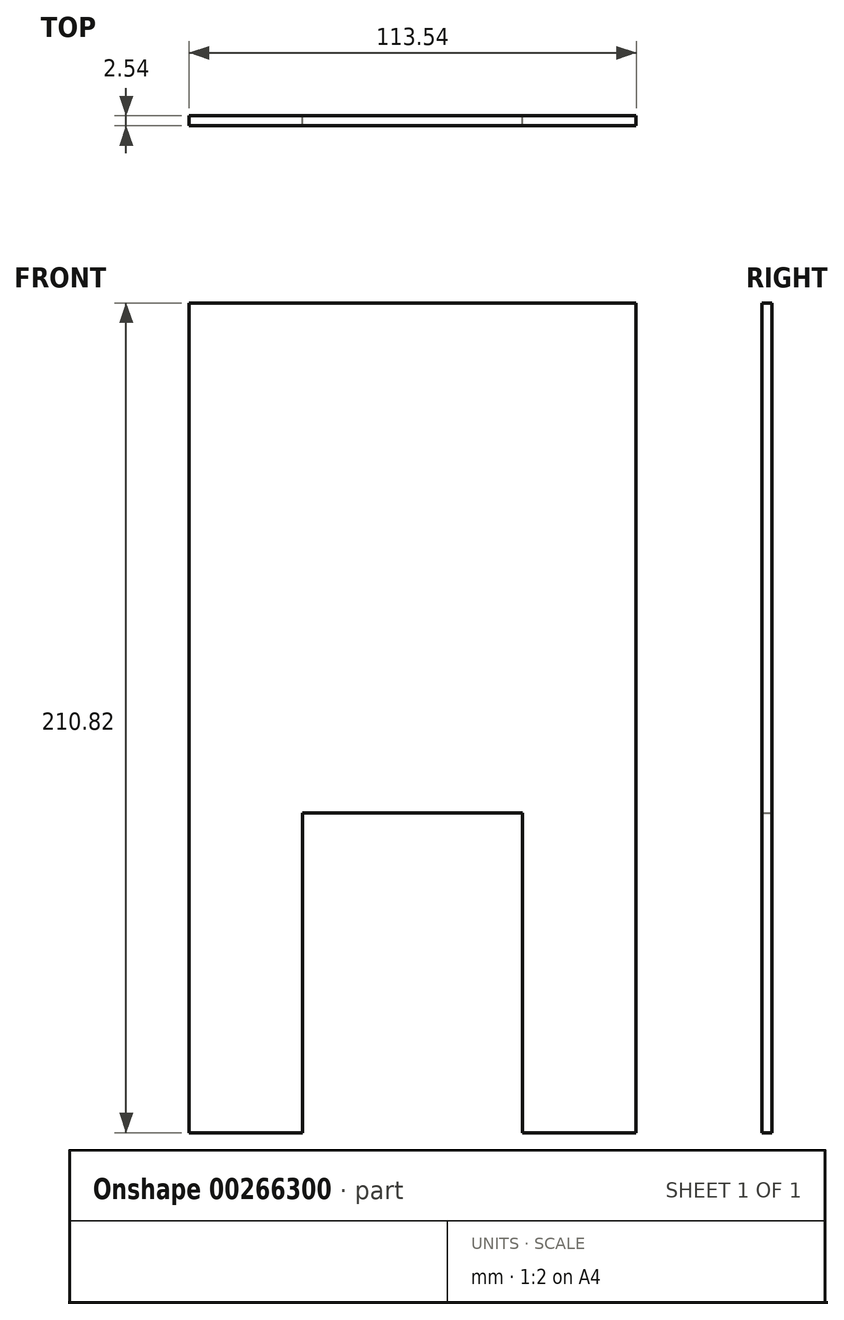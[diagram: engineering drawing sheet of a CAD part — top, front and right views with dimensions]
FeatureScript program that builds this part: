
annotation { "Feature Type Name" : "Feature", "Feature Type Description" : "" }
export const myFeature = defineFeature(function(context is Context, id is Id, definition is map)
    precondition{}
    {
        {
            var Q0;
            Q0=qCreatedBy(makeId("Front.planeOp"),FACE);
            var sketch = newSketch(context, id + "F0", { "sketchPlane" : qUnion([Q0])});
            skLineSegment(sketch, "E0", {"start": v(19.43, 0) * mm, "end": v(48.26, 0) * mm});
            skLineSegment(sketch, "E1", {"start": v(48.26, 0) * mm, "end": v(48.26, 81.28) * mm});
            skLineSegment(sketch, "E2", {"start": v(48.26, 81.28) * mm, "end": v(104.14, 81.28) * mm});
            skLineSegment(sketch, "E3", {"start": v(104.14, 81.28) * mm, "end": v(104.14, 0) * mm});
            skLineSegment(sketch, "E4", {"start": v(104.14, 0) * mm, "end": v(132.97, 0) * mm});
            skLineSegment(sketch, "E5", {"start": v(132.97, 210.82) * mm, "end": v(19.43, 210.82) * mm});
            skLineSegment(sketch, "E6", {"start": v(19.43, 40.64) * mm, "end": v(19.43, 91.44) * mm});
            skPoint(sketch, "E7.startSnap0", {"position": v(104.14, 40.64) * mm});
            skLineSegment(sketch, "E8", {"start": v(132.97, 40.64) * mm, "end": v(132.97, 91.44) * mm});
            skLineSegment(sketch, "E9", {"start": v(19.43, 129.54) * mm, "end": v(19.43, 180.34) * mm});
            skLineSegment(sketch, "E10", {"start": v(132.97, 129.54) * mm, "end": v(132.97, 180.34) * mm});
            skPoint(sketch, "E11.end.orphan", {"position": v(0, 180.34) * mm});
            skPoint(sketch, "E12.end.orphan", {"position": v(0, 91.44) * mm});
            skPoint(sketch, "E13.end.orphan", {"position": v(152.4, 40.64) * mm});
            skLineSegment(sketch, "E14", {"start": v(132.97, 40.64) * mm, "end": v(132.97, 0) * mm});
            skLineSegment(sketch, "E15", {"start": v(132.97, 0) * mm, "end": v(132.97, 91.44) * mm});
            skLineSegment(sketch, "E16", {"start": v(132.97, 129.54) * mm, "end": v(132.97, 91.44) * mm});
            skLineSegment(sketch, "E17", {"start": v(132.97, 180.34) * mm, "end": v(132.97, 210.82) * mm});
            skLineSegment(sketch, "E18", {"start": v(19.43, 180.34) * mm, "end": v(19.43, 0) * mm});
            skLineSegment(sketch, "E19", {"start": v(19.43, 0) * mm, "end": v(19.43, 210.82) * mm});
            skPoint(sketch, "E20.start.orphan", {"position": v(0, 210.82) * mm});
            skPoint(sketch, "E21.orphan", {"position": v(0, 0) * mm});
            skPoint(sketch, "E22.orphan", {"position": v(152.4, 0) * mm});
            skPoint(sketch, "E23.trimOffspring.end.orphan", {"position": v(152.4, 129.54) * mm});
            skSolve(sketch);
        }
        {
            var Q0;
            Q0=makeQuery(id+"F0.imprint","IMPRINT",FACE,{"disambiguationData":[TD([[makeQuery(id+"F0.imprint","IMPRINT",EDGE,{"derivedFrom":sQuery(id+"F0.wireOp",EDGE,"E0")}),1.0]])]});
            extrude(context, id + "F1", {"entities" : qUnion([Q0]), "depth" : 2.54 * mm});
        }
    });
